# Revit family: 400_57_BHT_Skyline_3000_80_(alu-rvs-pp_zwart-terra)_80-125
name_source: partatom
category: Air Terminals
revit_build: Autodesk Revit 2013 (Build: 20121003_2115(x64)
units: mm (PartAtom-declared; Revit-internal decimal feet)

## types (6) — shared parameters
Assembly Code = 3A(57)
IfcExportAs = IfcAirTerminal
IfcExportType = EYEBALL
Manufacturer = Burgerhout
Model = LOD400
Qv_exhaust_air = 0.0 L/s
Qv_supply_air = 0.0 L/s
URL = http://catalogus.burgerhout.nl
buitendiameter = 125 mm  [stored 0.410105 ft]
diameter = 80 mm  [stored 0.262467 ft]
lengte = 1360 mm  [stored 4.46194 ft]
max_medium_temperatuur = 120 °C
product_serie = Skyline 3000
werkende_lengte = 1340 mm  [stored 4.39633 ft]

## per-type parameters (varying)
| type | Description | EAN_code | GTIN_Code | IfcDescription | artikelnummer | buitenzijde_materiaal | gewicht_kg | materiaal | type_index |
| AL 80/125 zwart | Skyline 3000 Schoorsteentop HR AL CONC 80/125 zwart | 08712463023084 | 08712463023084 | Skyline 3000 Schoorsteentop HR AL CONC 80/125 zwart | 400452758 | BHT_aluminium_zwart | 4.2 kg | BHT_aluminium | 0 |
| RVS 80/125 zwart | Skyline 3000 Schoorsteentop HR RVS CONC 80/125 zwart | 08712463023091 | 08712463023091 | Skyline 3000 Schoorsteentop HR RVS CONC 80/125 zwart | 400452760 | BHT_aluminium_zwart | 3.74 kg | BHT_RVS | 1 |
| PP 80/125 zwart | Skyline 3000 Schoorsteentop HR PP CONC 80/125 zwart | 08712463023107 | 08712463023107 | Skyline 3000 Schoorsteentop HR PP CONC 80/125 zwart | 400452762 | BHT_aluminium_zwart | 3.48 kg | BHT_PP | 2 |
| AL 80/125 terra | Skyline 3000 Schoorsteentop HR AL CONC 80/125 terra | 08712463023114 | 08712463023114 | Skyline 3000 Schoorsteentop HR AL CONC 80/125 terra | 400452764 | BHT_aluminium_terra | 4.21 kg | BHT_aluminium | 3 |
| RVS 80/125 terra | Skyline 3000 Schoorsteentop HR RVS CONC 80/125 terra | 08712463023121 | 08712463023121 | Skyline 3000 Schoorsteentop HR RVS CONC 80/125 terra | 400452766 | BHT_aluminium_terra | 3.71 kg | BHT_RVS | 4 |
| PP 80/125 terra | Skyline 3000 Schoorsteentop HR PP CONC 80/125 terra | 08712463023138 | 08712463023138 | Skyline 3000 Schoorsteentop HR PP CONC 80/125 terra | 400452768 | BHT_aluminium_terra | 3.41 kg | BHT_PP | 5 |

note: [stored X ft] marks values corroborated as IEEE doubles in the binary element streams (Revit-internal decimal feet)

## geometry (parser evidence)
native form markers: Blend x12, Sweep x1
no freeform markers — native parametric forms only
